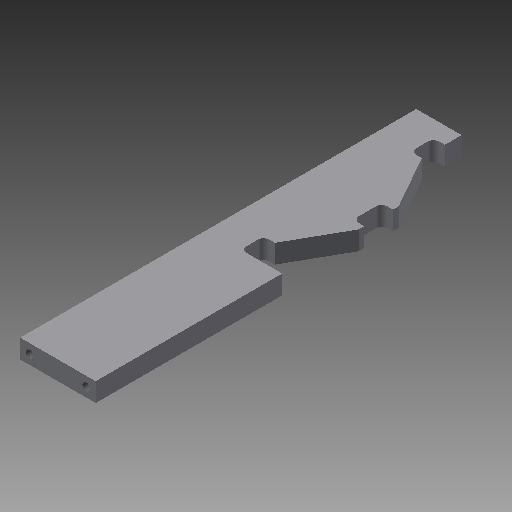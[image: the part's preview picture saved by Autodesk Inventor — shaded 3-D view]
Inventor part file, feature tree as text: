
AUTODESK INVENTOR PART (.ipt)
format: ipt  version: 2018 (Build 220112000, 112)  size: 154,112 bytes
history: native  units: mm
features: extrude x3, hole x1
ambient origin geometry x8: Origin, YZ Plane, XZ Plane, XY Plane, X Axis, Y Axis, Z Axis, Center Point
bodies: Volumenkörper1 (feature_tree)
feature tree (4):
  extrude  "Extrusion1"  Depth=210.0mm
  extrude  "Extrusion2"  Depth=40.0mm
  extrude  "Extrusion3"  Depth=10.0mm TaperAngle=0.0deg
  hole  "Bohrung1"  [1 undecoded]
note: 1 required parameter value undecoded (feature->parameter linkage not recoverable at this tier; creation-order binding heuristic only, values carry confidence <= 0.55)
